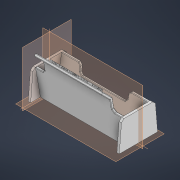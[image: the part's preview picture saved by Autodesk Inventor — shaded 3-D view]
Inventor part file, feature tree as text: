
AUTODESK INVENTOR PART (.ipt)
format: ipt  version: 2021 (Build 250183000, 183)  size: 3,987,456 bytes
history: native  units: mm
features: other x5, extrude x5, sketch x4, chamfer x2, move_body x2, fillet x1, mirror x1
ambient origin geometry x8: Origin, YZ Plane, XZ Plane, XY Plane, X Axis, Y Axis, Z Axis, Center Point
bodies: Solid1 (feature_tree)
feature tree (20):
  other  "Blocks"
  extrude  "Extrusion1"  Depth=35.0mm
  extrude  "Extrusion2"  TaperAngle=0.0deg  [1 undecoded]
  extrude  "Extrusion5"  Depth=2.5mm
  extrude  "Extrusion6"  Depth=2.5mm
  fillet  "Fillet1"  Radius=2.5mm
  mirror  "Mirror1"
  extrude  "Extrusion8"  Depth=2.5mm
  chamfer  "Chamfer1"  Distance=17.453293mm
  chamfer  "Chamfer2"  Distance=17.453293mm
  move_body  "Move Body1"
  move_body  "Move Body2"
  sketch  "Sketch2"  dims[d4=30.0mm d5=35.0mm]
  sketch  "Sketch5"  dims[d6=40.0mm d14=0.0mm]
  sketch  "Sketch8"  dims[d15=2.5mm d16=2.5mm]
  other  "Block1"
  sketch  "Sketch15"  dims[d17=2.5mm d18=2.5mm d19=2.5mm d20=40.0mm d22=17.453293mm d23=17.453293mm d24=45.0mm d25=0.0mm d33=10.0mm d34=25.0mm d35=2.5mm d36=0.0mm d38=10.0mm d39=2.5mm d40=0.0mm d41=2.5mm d43=2.5mm d45=45.0deg d46=10.0mm d47=100.0mm d60=1.5mm d61=0.0mm d62=2.5mm d63=2.0mm d64=45.0deg d65=0.5mm d66=2.0mm d67=45.0deg d68=90.0deg d69=180.0deg]
  other  "lgcc"
  other  "lgcc2"
  other  "lgcc2:1"
note: 1 required parameter value undecoded (feature->parameter linkage not recoverable at this tier; creation-order binding heuristic only, values carry confidence <= 0.55)
